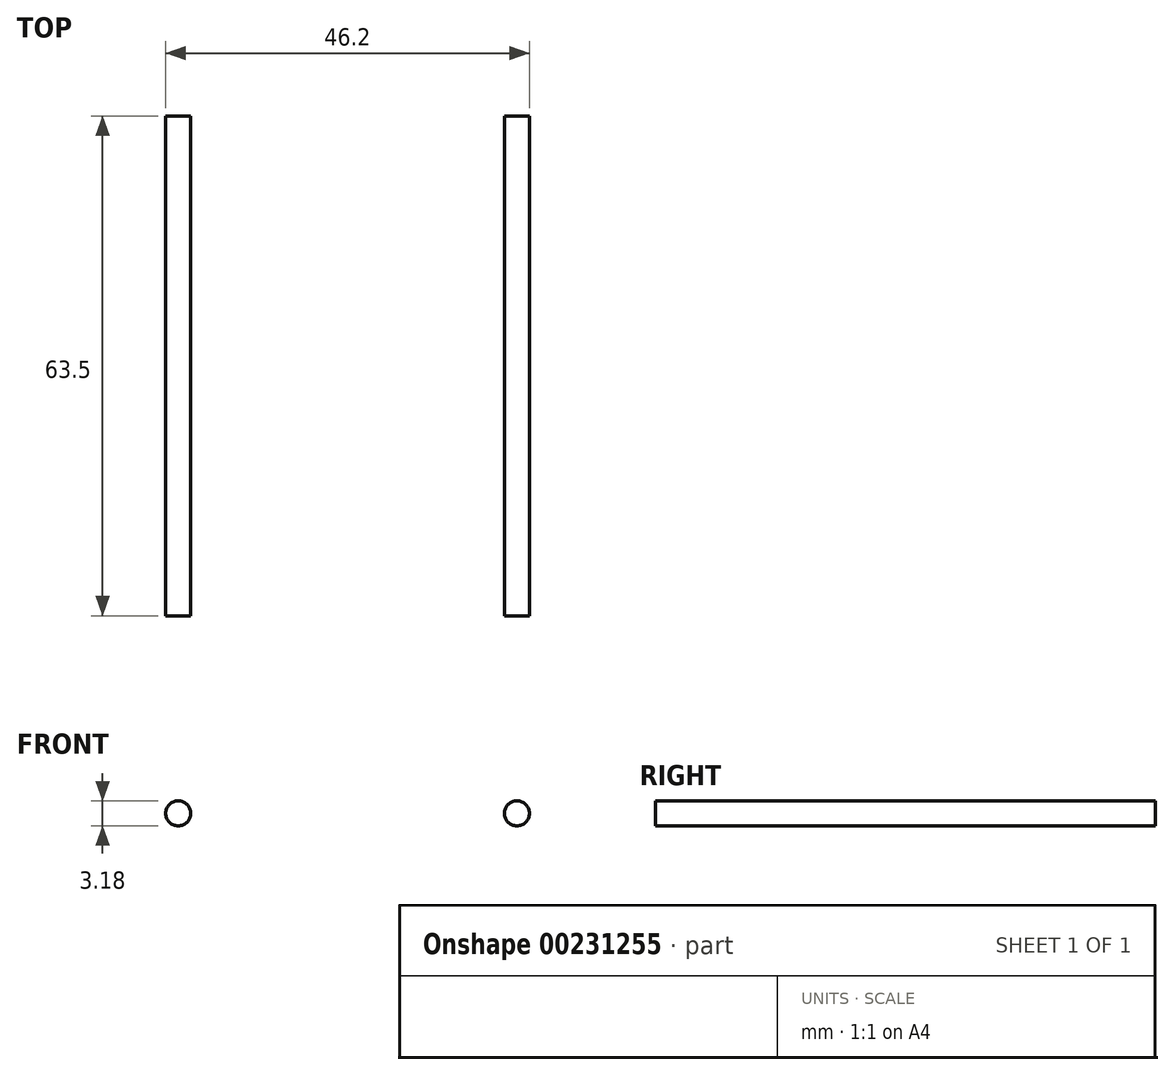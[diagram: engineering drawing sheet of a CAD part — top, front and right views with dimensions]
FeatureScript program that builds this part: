
annotation { "Feature Type Name" : "Feature", "Feature Type Description" : "" }
export const myFeature = defineFeature(function(context is Context, id is Id, definition is map)
    precondition{}
    {
        {
            var Q0;
            Q0=qCreatedBy(makeId("Front.planeOp"),FACE);
            var sketch = newSketch(context, id + "F0", { "sketchPlane" : qUnion([Q0])});
            skCircle(sketch, "E0", {"center": v(-24.17, 0) * mm, "radius": 1.59 * mm});
            skCircle(sketch, "E1", {"center": v(18.85, 0) * mm, "radius": 1.59 * mm});
            skSolve(sketch);
        }
        {
            var Q0;
            Q0=qSketchRegion(id+"F0",true);
            extrude(context, id + "F1", {"entities" : qUnion([Q0]), "depth" : 63.5 * mm});
        }
    });
